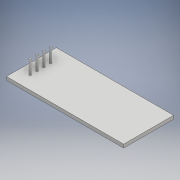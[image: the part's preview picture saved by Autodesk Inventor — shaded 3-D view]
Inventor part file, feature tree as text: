
AUTODESK INVENTOR PART (.ipt)
format: ipt  version: 2018.3 (Build 223284000, 284)  size: 106,496 bytes
history: native  units: mm
features: extrude x2, sketch x2
ambient origin geometry x8: Origin, YZ Plane, XZ Plane, XY Plane, X Axis, Y Axis, Z Axis, Center Point
bodies: Solid1 (feature_tree)
feature tree (4):
  extrude  "Extrusion1"  Depth=34.5mm
  extrude  "Extrusion3"  Depth=4.0mm
  sketch  "Sketch1"  dims[d0=14.7mm d1=34.5mm]
  sketch  "Sketch3"  dims[d2=1.0mm d3=0.0mm d9=0.65mm d10=0.65mm d11=0.65mm d12=0.65mm d13=4.0mm d14=0.0mm]
